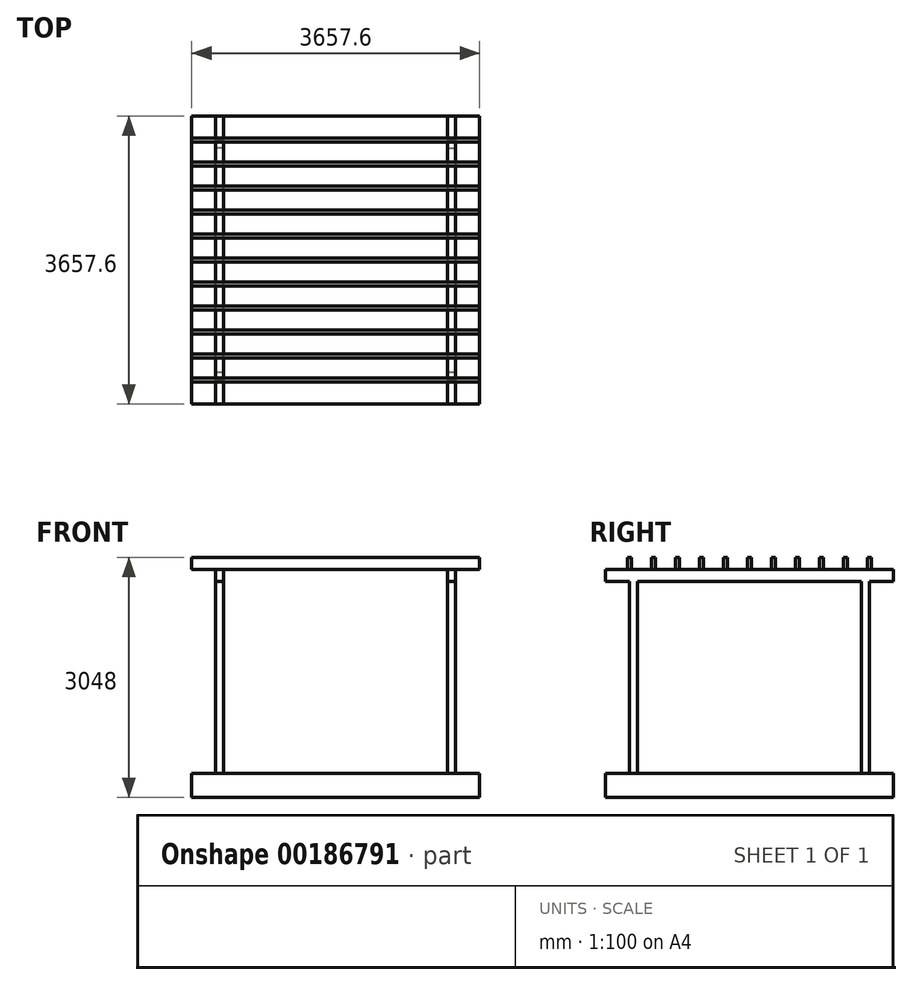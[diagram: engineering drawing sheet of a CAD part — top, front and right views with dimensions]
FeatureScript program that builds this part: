
annotation { "Feature Type Name" : "Feature", "Feature Type Description" : "" }
export const myFeature = defineFeature(function(context is Context, id is Id, definition is map)
    precondition{}
    {
        {
            var Q0;
            Q0=qCreatedBy(makeId("Top.planeOp"),FACE);
            var sketch = newSketch(context, id + "F0", { "sketchPlane" : qUnion([Q0])});
            skLineSegment(sketch, "E0.bottom", {"start": v(-1828.8, -1828.8) * mm, "end": v(1828.8, -1828.8) * mm});
            skLineSegment(sketch, "E0.top", {"start": v(-1828.8, 1828.8) * mm, "end": v(1828.8, 1828.8) * mm});
            skLineSegment(sketch, "E0.left", {"start": v(-1828.8, -1828.8) * mm, "end": v(-1828.8, 1828.8) * mm});
            skLineSegment(sketch, "E0.right", {"start": v(1828.8, -1828.8) * mm, "end": v(1828.8, 1828.8) * mm});
            skPoint(sketch, "E0.middle", {"position": v(0, 0) * mm});
            skSolve(sketch);
        }
        {
            var Q0;
            Q0 = qSketchRegion(id + "F0", true);
            extrude(context, id + "F1", {"entities" : qUnion([Q0]), "oppositeDirection" : true, "depth" : 304.8 * mm});
        }
        {
            var Q0;
            Q0=makeQuery(id+"F1.opExtrude","CAP_FACE",FACE,{"disambiguationData":[OSD([sQuery(id+"F0.wireOp",EDGE,"E0.bottom"),sQuery(id+"F0.wireOp",EDGE,"E0.top"),sQuery(id+"F0.wireOp",EDGE,"E0.left"),sQuery(id+"F0.wireOp",EDGE,"E0.right")])],"isStart":true});
            var sketch = newSketch(context, id + "F2", { "sketchPlane" : qUnion([Q0])});
            skLineSegment(sketch, "E1.bottom", {"start": v(-1422.4, 1422.4) * mm, "end": v(-1524, 1422.4) * mm});
            skLineSegment(sketch, "E1.top", {"start": v(-1422.4, 1524) * mm, "end": v(-1524, 1524) * mm});
            skLineSegment(sketch, "E1.left", {"start": v(-1422.4, 1422.4) * mm, "end": v(-1422.4, 1524) * mm});
            skLineSegment(sketch, "E1.right", {"start": v(-1524, 1422.4) * mm, "end": v(-1524, 1524) * mm});
            skPoint(sketch, "E1.middle", {"position": v(-1473.2, 1473.2) * mm});
            skLineSegment(sketch, "E2.bottom", {"start": v(1422.4, 1524) * mm, "end": v(1524, 1524) * mm});
            skLineSegment(sketch, "E2.top", {"start": v(1422.4, 1422.4) * mm, "end": v(1524, 1422.4) * mm});
            skLineSegment(sketch, "E2.left", {"start": v(1422.4, 1524) * mm, "end": v(1422.4, 1422.4) * mm});
            skLineSegment(sketch, "E2.right", {"start": v(1524, 1524) * mm, "end": v(1524, 1422.4) * mm});
            skPoint(sketch, "E2.middle", {"position": v(1473.2, 1473.2) * mm});
            skLineSegment(sketch, "E3.bottom", {"start": v(1422.4, -1422.4) * mm, "end": v(1524, -1422.4) * mm});
            skLineSegment(sketch, "E3.top", {"start": v(1422.4, -1524) * mm, "end": v(1524, -1524) * mm});
            skLineSegment(sketch, "E3.left", {"start": v(1422.4, -1422.4) * mm, "end": v(1422.4, -1524) * mm});
            skLineSegment(sketch, "E3.right", {"start": v(1524, -1422.4) * mm, "end": v(1524, -1524) * mm});
            skPoint(sketch, "E3.middle", {"position": v(1473.2, -1473.2) * mm});
            skLineSegment(sketch, "E4.bottom", {"start": v(-1524, -1422.4) * mm, "end": v(-1422.4, -1422.4) * mm});
            skLineSegment(sketch, "E4.top", {"start": v(-1524, -1524) * mm, "end": v(-1422.4, -1524) * mm});
            skLineSegment(sketch, "E4.left", {"start": v(-1524, -1422.4) * mm, "end": v(-1524, -1524) * mm});
            skLineSegment(sketch, "E4.right", {"start": v(-1422.4, -1422.4) * mm, "end": v(-1422.4, -1524) * mm});
            skPoint(sketch, "E4.middle", {"position": v(-1473.2, -1473.2) * mm});
            skSolve(sketch);
        }
        {
            var Q0;
            Q0 = qSketchRegion(id + "F2", true);
            extrude(context, id + "F3", {"entities" : qUnion([Q0]), "operationType" : NewBodyOperationType.ADD, "depth" : 2438.4 * mm});
        }
        {
            var Q0;
            Q0=makeQuery(id+"F3.opExtrude","CAP_FACE",FACE,{"disambiguationData":[OSD([sQuery(id+"F2.wireOp",EDGE,"E4.bottom"),sQuery(id+"F2.wireOp",EDGE,"E4.top"),sQuery(id+"F2.wireOp",EDGE,"E4.left"),sQuery(id+"F2.wireOp",EDGE,"E4.right")])],"isStart":false});
            var sketch = newSketch(context, id + "F4", { "sketchPlane" : qUnion([Q0])});
            skLineSegment(sketch, "E5.bottom", {"start": v(-1524, -1828.8) * mm, "end": v(-1422.4, -1828.8) * mm});
            skLineSegment(sketch, "E5.top", {"start": v(-1524, 1828.8) * mm, "end": v(-1422.4, 1828.8) * mm});
            skLineSegment(sketch, "E5.left", {"start": v(-1524, -1828.8) * mm, "end": v(-1524, 1828.8) * mm});
            skLineSegment(sketch, "E5.right", {"start": v(-1422.4, -1828.8) * mm, "end": v(-1422.4, 1828.8) * mm});
            skLineSegment(sketch, "E6.bottom", {"start": v(1422.4, 1828.8) * mm, "end": v(1524, 1828.8) * mm});
            skLineSegment(sketch, "E6.top", {"start": v(1422.4, -1828.8) * mm, "end": v(1524, -1828.8) * mm});
            skLineSegment(sketch, "E6.left", {"start": v(1422.4, 1828.8) * mm, "end": v(1422.4, -1828.8) * mm});
            skLineSegment(sketch, "E6.right", {"start": v(1524, 1828.8) * mm, "end": v(1524, -1828.8) * mm});
            skSolve(sketch);
        }
        {
            var Q0;
            Q0 = qSketchRegion(id + "F4", true);
            extrude(context, id + "F5", {"entities" : qUnion([Q0]), "operationType" : NewBodyOperationType.ADD, "depth" : 152.4 * mm});
        }
        {
            var Q0;
            Q0=makeQuery(id+"F5.opExtrude","CAP_FACE",FACE,{"disambiguationData":[OSD([sQuery(id+"F4.wireOp",EDGE,"E5.bottom"),sQuery(id+"F4.wireOp",EDGE,"E5.top"),sQuery(id+"F4.wireOp",EDGE,"E5.left"),sQuery(id+"F4.wireOp",EDGE,"E5.right")])],"isStart":false});
            var sketch = newSketch(context, id + "F6", { "sketchPlane" : qUnion([Q0])});
            skLineSegment(sketch, "E7.bottom", {"start": v(-1828.8, -1549.4) * mm, "end": v(1828.8, -1549.4) * mm});
            skLineSegment(sketch, "E7.top", {"start": v(-1828.8, -1498.6) * mm, "end": v(1828.8, -1498.6) * mm});
            skLineSegment(sketch, "E7.left", {"start": v(-1828.8, -1549.4) * mm, "end": v(-1828.8, -1498.6) * mm});
            skLineSegment(sketch, "E7.right", {"start": v(1828.8, -1549.4) * mm, "end": v(1828.8, -1498.6) * mm});
            skLineSegment(sketch, "E8.0.1.0", {"start": v(-1828.8, -1244.6) * mm, "end": v(1828.8, -1244.6) * mm});
            skLineSegment(sketch, "E8.0.1.1", {"start": v(-1828.8, -1244.6) * mm, "end": v(-1828.8, -1193.8) * mm});
            skLineSegment(sketch, "E8.0.1.2", {"start": v(-1828.8, -1193.8) * mm, "end": v(1828.8, -1193.8) * mm});
            skLineSegment(sketch, "E8.0.1.3", {"start": v(1828.8, -1244.6) * mm, "end": v(1828.8, -1193.8) * mm});
            skLineSegment(sketch, "E8.0.2.0", {"start": v(-1828.8, -939.8) * mm, "end": v(1828.8, -939.8) * mm});
            skLineSegment(sketch, "E8.0.2.1", {"start": v(-1828.8, -939.8) * mm, "end": v(-1828.8, -889) * mm});
            skLineSegment(sketch, "E8.0.2.2", {"start": v(-1828.8, -889) * mm, "end": v(1828.8, -889) * mm});
            skLineSegment(sketch, "E8.0.2.3", {"start": v(1828.8, -939.8) * mm, "end": v(1828.8, -889) * mm});
            skLineSegment(sketch, "E8.0.3.0", {"start": v(-1828.8, -635) * mm, "end": v(1828.8, -635) * mm});
            skLineSegment(sketch, "E8.0.3.1", {"start": v(-1828.8, -635) * mm, "end": v(-1828.8, -584.2) * mm});
            skLineSegment(sketch, "E8.0.3.2", {"start": v(-1828.8, -584.2) * mm, "end": v(1828.8, -584.2) * mm});
            skLineSegment(sketch, "E8.0.3.3", {"start": v(1828.8, -635) * mm, "end": v(1828.8, -584.2) * mm});
            skLineSegment(sketch, "E8.0.4.0", {"start": v(-1828.8, -330.2) * mm, "end": v(1828.8, -330.2) * mm});
            skLineSegment(sketch, "E8.0.4.1", {"start": v(-1828.8, -330.2) * mm, "end": v(-1828.8, -279.4) * mm});
            skLineSegment(sketch, "E8.0.4.2", {"start": v(-1828.8, -279.4) * mm, "end": v(1828.8, -279.4) * mm});
            skLineSegment(sketch, "E8.0.4.3", {"start": v(1828.8, -330.2) * mm, "end": v(1828.8, -279.4) * mm});
            skLineSegment(sketch, "E8.0.5.0", {"start": v(-1828.8, -25.4) * mm, "end": v(1828.8, -25.4) * mm});
            skLineSegment(sketch, "E8.0.5.1", {"start": v(-1828.8, -25.4) * mm, "end": v(-1828.8, 25.4) * mm});
            skLineSegment(sketch, "E8.0.5.2", {"start": v(-1828.8, 25.4) * mm, "end": v(1828.8, 25.4) * mm});
            skLineSegment(sketch, "E8.0.5.3", {"start": v(1828.8, -25.4) * mm, "end": v(1828.8, 25.4) * mm});
            skLineSegment(sketch, "E8.0.6.0", {"start": v(-1828.8, 279.4) * mm, "end": v(1828.8, 279.4) * mm});
            skLineSegment(sketch, "E8.0.6.1", {"start": v(-1828.8, 279.4) * mm, "end": v(-1828.8, 330.2) * mm});
            skLineSegment(sketch, "E8.0.6.2", {"start": v(-1828.8, 330.2) * mm, "end": v(1828.8, 330.2) * mm});
            skLineSegment(sketch, "E8.0.6.3", {"start": v(1828.8, 279.4) * mm, "end": v(1828.8, 330.2) * mm});
            skLineSegment(sketch, "E8.0.7.0", {"start": v(-1828.8, 584.2) * mm, "end": v(1828.8, 584.2) * mm});
            skLineSegment(sketch, "E8.0.7.1", {"start": v(-1828.8, 584.2) * mm, "end": v(-1828.8, 635) * mm});
            skLineSegment(sketch, "E8.0.7.2", {"start": v(-1828.8, 635) * mm, "end": v(1828.8, 635) * mm});
            skLineSegment(sketch, "E8.0.7.3", {"start": v(1828.8, 584.2) * mm, "end": v(1828.8, 635) * mm});
            skLineSegment(sketch, "E8.0.8.0", {"start": v(-1828.8, 889) * mm, "end": v(1828.8, 889) * mm});
            skLineSegment(sketch, "E8.0.8.1", {"start": v(-1828.8, 889) * mm, "end": v(-1828.8, 939.8) * mm});
            skLineSegment(sketch, "E8.0.8.2", {"start": v(-1828.8, 939.8) * mm, "end": v(1828.8, 939.8) * mm});
            skLineSegment(sketch, "E8.0.8.3", {"start": v(1828.8, 889) * mm, "end": v(1828.8, 939.8) * mm});
            skLineSegment(sketch, "E8.0.9.0", {"start": v(-1828.8, 1193.8) * mm, "end": v(1828.8, 1193.8) * mm});
            skLineSegment(sketch, "E8.0.9.1", {"start": v(-1828.8, 1193.8) * mm, "end": v(-1828.8, 1244.6) * mm});
            skLineSegment(sketch, "E8.0.9.2", {"start": v(-1828.8, 1244.6) * mm, "end": v(1828.8, 1244.6) * mm});
            skLineSegment(sketch, "E8.0.9.3", {"start": v(1828.8, 1193.8) * mm, "end": v(1828.8, 1244.6) * mm});
            skLineSegment(sketch, "E8.0.10.0", {"start": v(-1828.8, 1498.6) * mm, "end": v(1828.8, 1498.6) * mm});
            skLineSegment(sketch, "E8.0.10.1", {"start": v(-1828.8, 1498.6) * mm, "end": v(-1828.8, 1549.4) * mm});
            skLineSegment(sketch, "E8.0.10.2", {"start": v(-1828.8, 1549.4) * mm, "end": v(1828.8, 1549.4) * mm});
            skLineSegment(sketch, "E8.0.10.3", {"start": v(1828.8, 1498.6) * mm, "end": v(1828.8, 1549.4) * mm});
            skLineSegment(sketch, "E8.direction1", {"start": v(-1828.8, -1498.6) * mm, "end": v(-1803.4, -1498.6) * mm, "construction": true});
            skLineSegment(sketch, "E8.direction2", {"start": v(-1828.8, -1498.6) * mm, "end": v(-1828.8, -1193.8) * mm, "construction": true});
            skSolve(sketch);
        }
        {
            var Q0;
            Q0 = qSketchRegion(id + "F6", true);
            extrude(context, id + "F7", {"entities" : qUnion([Q0]), "operationType" : NewBodyOperationType.ADD, "depth" : 152.4 * mm});
        }
    });
